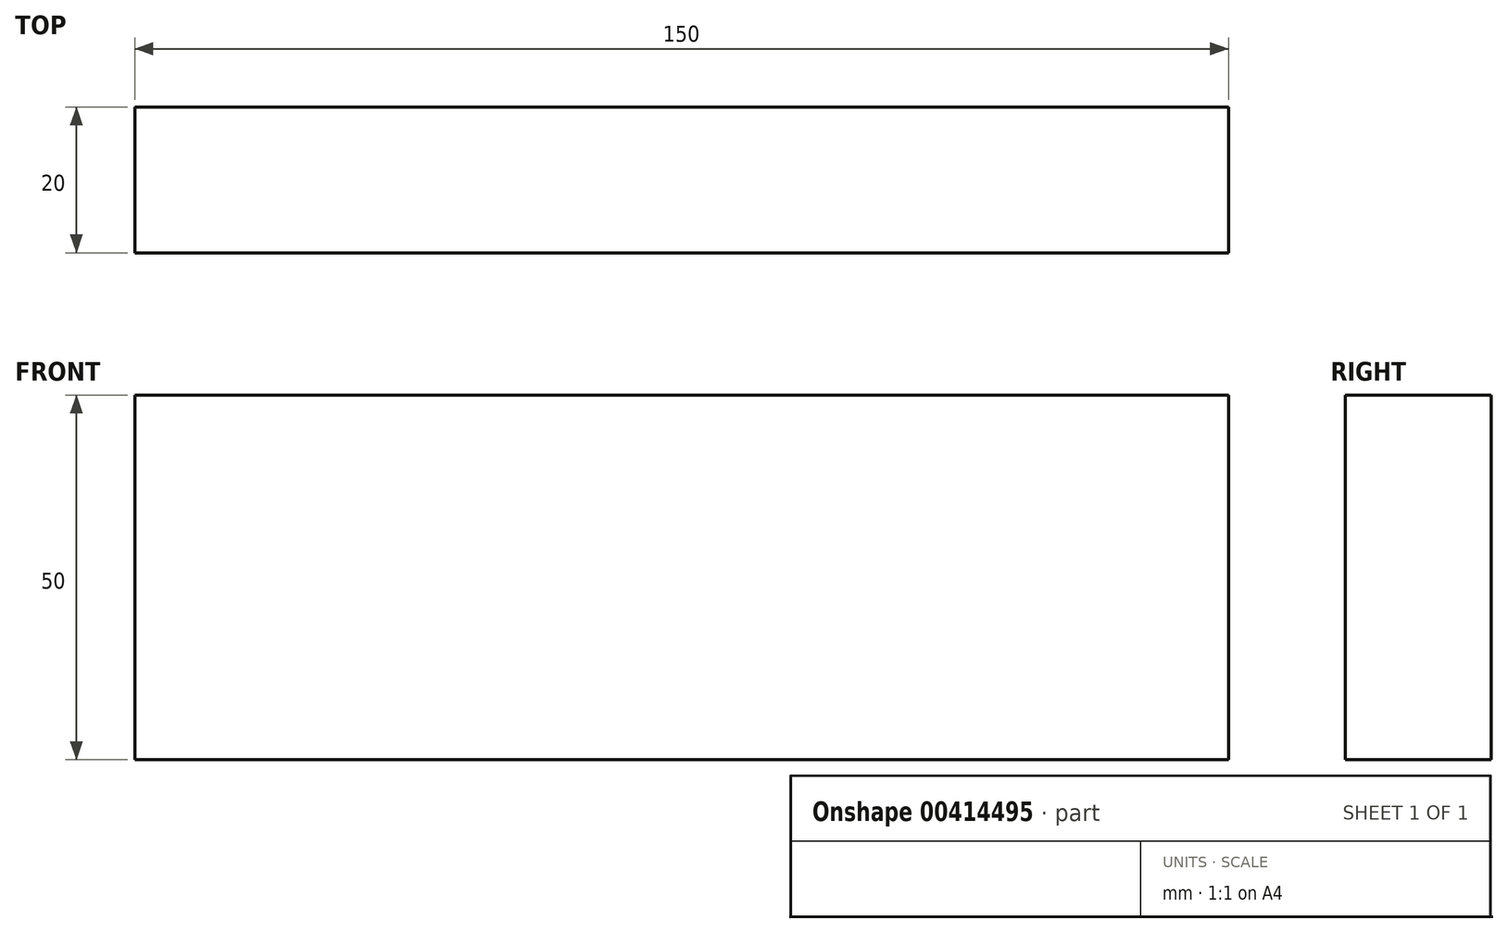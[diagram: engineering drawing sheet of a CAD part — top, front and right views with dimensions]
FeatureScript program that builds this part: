
annotation { "Feature Type Name" : "Feature", "Feature Type Description" : "" }
export const myFeature = defineFeature(function(context is Context, id is Id, definition is map)
    precondition{}
    {
        {
            var Q0;
            Q0=qCreatedBy(makeId("Top.planeOp"),FACE);
            var sketch = newSketch(context, id + "F0", { "sketchPlane" : qUnion([Q0])});
            skLineSegment(sketch, "E0.bottom", {"start": v(0, 0) * mm, "end": v(150, 0) * mm});
            skLineSegment(sketch, "E0.top", {"start": v(0, 20) * mm, "end": v(150, 20) * mm});
            skLineSegment(sketch, "E0.left", {"start": v(0, 0) * mm, "end": v(0, 20) * mm});
            skLineSegment(sketch, "E0.right", {"start": v(150, 0) * mm, "end": v(150, 20) * mm});
            skSolve(sketch);
        }
        {
            var Q0;
            Q0=makeQuery(id+"F0.imprint","IMPRINT",FACE,{"disambiguationData":[TD([[makeQuery(id+"F0.imprint","IMPRINT",EDGE,{"derivedFrom":sQuery(id+"F0.wireOp",EDGE,"E0.bottom")}),1.0]])]});
            extrude(context, id + "F1", {"entities" : qUnion([Q0]), "depth" : 50 * mm, "offsetDistance" : 25 * mm});
        }
    });
